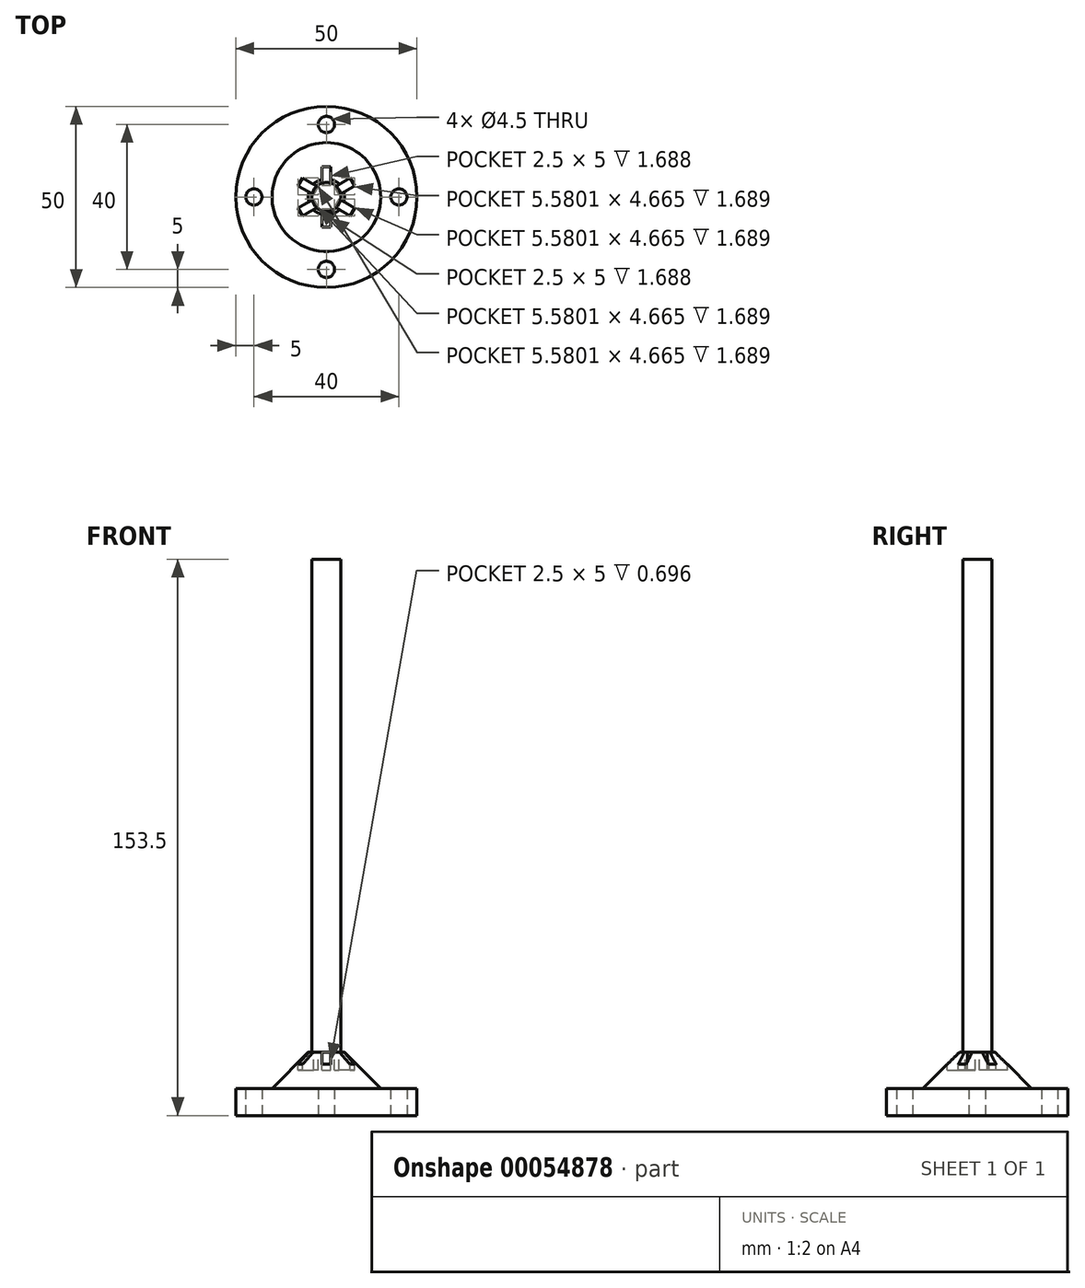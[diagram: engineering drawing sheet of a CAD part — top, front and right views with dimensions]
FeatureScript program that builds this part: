
annotation { "Feature Type Name" : "Feature", "Feature Type Description" : "" }
export const myFeature = defineFeature(function(context is Context, id is Id, definition is map)
    precondition{}
    {
        {
            var Q0;
            Q0=qCreatedBy(makeId("Top.planeOp"),FACE);
            var sketch = newSketch(context, id + "F0", { "sketchPlane" : qUnion([Q0])});
            skCircle(sketch, "E0", {"center": v(0, 0) * mm, "radius": 4 * mm});
            skSolve(sketch);
        }
        {
            var Q0;
            Q0=makeQuery(id+"F0.imprint","IMPRINT",FACE,{"disambiguationData":[TD([[makeQuery(id+"F0.imprint","IMPRINT",EDGE,{"derivedFrom":sQuery(id+"F0.wireOp",EDGE,"E0")}),1.0]])]});
            extrude(context, id + "F1", {"entities" : qUnion([Q0]), "depth" : 136 * mm});
        }
        {
            var Q0;
            Q0=qCreatedBy(makeId("Top.planeOp"),FACE);
            var sketch = newSketch(context, id + "F2", { "sketchPlane" : qUnion([Q0])});
            skCircle(sketch, "E1", {"center": v(0, 0) * mm, "radius": 15 * mm});
            skSolve(sketch);
        }
        {
            var Q0;
            Q0=makeQuery(id+"F2.imprint","IMPRINT",FACE,{"disambiguationData":[TD([[makeQuery(id+"F2.imprint","IMPRINT",EDGE,{"derivedFrom":sQuery(id+"F2.wireOp",EDGE,"E1")}),1.0]])]});
            extrude(context, id + "F3", {"entities" : qUnion([Q0]), "operationType" : NewBodyOperationType.ADD, "oppositeDirection" : true, "depth" : 10 * mm});
        }
        {
            var Q0;
            Q0=makeQuery(id+"F3.opExtrude","CAP_EDGE",EDGE,{"disambiguationData":[OSD([sQuery(id+"F2.wireOp",EDGE,"E1")])],"isStart":true});
            chamfer(context, id + "F4", {"entities" : qUnion([Q0]), "width" : 10 * mm, "tangentPropagation" : true});
        }
        {
            var Q0;
            Q0=makeQuery(id+"F3.opExtrude","CAP_FACE",FACE,{"disambiguationData":[OSD([sQuery(id+"F2.wireOp",EDGE,"E1")])],"isStart":false});
            var sketch = newSketch(context, id + "F5", { "sketchPlane" : qUnion([Q0])});
            skCircle(sketch, "E2", {"center": v(0, 0) * mm, "radius": 25 * mm});
            skSolve(sketch);
        }
        {
            var Q0;
            Q0=makeQuery(id+"F5.imprint","IMPRINT",FACE,{"disambiguationData":[TD([[makeQuery(id+"F5.imprint","IMPRINT",EDGE,{"derivedFrom":sQuery(id+"F5.wireOp",EDGE,"E2")}),1.0]])]});
            var Q1;
            {var subQ0=sQuery(id+"F2.wireOp",EDGE,"E1");Q1=makeQuery(id+"F5.imprint","IMPRINT",FACE,{"disambiguationData":[TD([[makeQuery(id+"F5.imprint","IMPRINT",EDGE,{"derivedFrom":makeQuery(id+"F4.opChamfer","BLEND_EDGE",EDGE,{"blendedFrom":[makeQuery(id+"F3.opExtrude","CAP_EDGE",EDGE,{"disambiguationData":[OSD([subQ0])],"isStart":true}),makeQuery(id+"F3.opExtrude","CAP_FACE",FACE,{"disambiguationData":[OSD([subQ0])],"isStart":false})],"blendedInto":[makeQuery(id+"F3.opExtrude","CAP_FACE",FACE,{"disambiguationData":[OSD([subQ0])],"isStart":false})]})}),-1.0]])]});}
            extrude(context, id + "F6", {"entities" : qUnion([Q0, Q1]), "depth" : 7.5 * mm});
        }
        {
            var Q0;
            Q0=makeQuery(id+"F6.opExtrude","CAP_FACE",FACE,{"disambiguationData":[OSD([sQuery(id+"F2.wireOp",EDGE,"E1"),sQuery(id+"F5.wireOp",EDGE,"E2")])],"isStart":false});
            var sketch = newSketch(context, id + "F7", { "sketchPlane" : qUnion([Q0])});
            skCircle(sketch, "E3", {"center": v(0, 20) * mm, "radius": 2.25 * mm});
            skCircle(sketch, "E4.1.0", {"center": v(20, 0) * mm, "radius": 2.25 * mm});
            skCircle(sketch, "E4.2.0", {"center": v(0, -20) * mm, "radius": 2.25 * mm});
            skPoint(sketch, "E4.center", {"position": v(0, 0) * mm});
            skLineSegment(sketch, "E4.anchor1", {"start": v(0, 0) * mm, "end": v(0, 20) * mm, "construction": true});
            skLineSegment(sketch, "E4.anchor2", {"start": v(0, 0) * mm, "end": v(-20, 0) * mm, "construction": true});
            skCircle(sketch, "E5.1.3.0", {"center": v(-20, 0) * mm, "radius": 2.25 * mm});
            skSolve(sketch);
        }
        {
            var Q0;
            Q0=makeQuery(id+"F7.imprint","IMPRINT",FACE,{"disambiguationData":[TD([[makeQuery(id+"F7.imprint","IMPRINT",EDGE,{"derivedFrom":sQuery(id+"F7.wireOp",EDGE,"E5.1.3.0")}),1.0]])]});
            var Q1;
            Q1=makeQuery(id+"F7.imprint","IMPRINT",FACE,{"disambiguationData":[TD([[makeQuery(id+"F7.imprint","IMPRINT",EDGE,{"derivedFrom":sQuery(id+"F7.wireOp",EDGE,"E3")}),1.0]])]});
            var Q2;
            Q2=makeQuery(id+"F7.imprint","IMPRINT",FACE,{"disambiguationData":[TD([[makeQuery(id+"F7.imprint","IMPRINT",EDGE,{"derivedFrom":sQuery(id+"F7.wireOp",EDGE,"E4.1.0")}),1.0]])]});
            var Q3;
            Q3=makeQuery(id+"F7.imprint","IMPRINT",FACE,{"disambiguationData":[TD([[makeQuery(id+"F7.imprint","IMPRINT",EDGE,{"derivedFrom":sQuery(id+"F7.wireOp",EDGE,"E4.2.0")}),1.0]])]});
            extrude(context, id + "F8", {"entities" : qUnion([Q0, Q1, Q2, Q3]), "operationType" : NewBodyOperationType.REMOVE, "endBound" : BoundingType.THROUGH_ALL, "oppositeDirection" : true, "depth" : 25 * mm});
        }
        {
            var Q0;
            Q0=makeQuery(id+"F3.opExtrude","CAP_FACE",FACE,{"disambiguationData":[OSD([sQuery(id+"F2.wireOp",EDGE,"E1")])],"isStart":true});
            var sketch = newSketch(context, id + "F9", { "sketchPlane" : qUnion([Q0])});
            skLineSegment(sketch, "E6.bottom", {"start": v(-1.25, 8.3) * mm, "end": v(1.25, 8.3) * mm});
            skLineSegment(sketch, "E6.top", {"start": v(-1.25, 3.3) * mm, "end": v(1.25, 3.3) * mm});
            skLineSegment(sketch, "E6.left", {"start": v(-1.25, 8.3) * mm, "end": v(-1.25, 3.3) * mm});
            skLineSegment(sketch, "E6.right", {"start": v(1.25, 8.3) * mm, "end": v(1.25, 3.3) * mm});
            skLineSegment(sketch, "E7.1.0", {"start": v(-6.56, 5.23) * mm, "end": v(-2.23, 2.73) * mm});
            skLineSegment(sketch, "E7.1.1", {"start": v(-7.81, 3.07) * mm, "end": v(-3.48, 0.57) * mm});
            skLineSegment(sketch, "E7.1.2", {"start": v(-3.48, 0.57) * mm, "end": v(-2.23, 2.73) * mm});
            skLineSegment(sketch, "E7.1.3", {"start": v(-7.81, 3.07) * mm, "end": v(-6.56, 5.23) * mm});
            skLineSegment(sketch, "E7.2.0", {"start": v(-7.81, -3.07) * mm, "end": v(-3.48, -0.57) * mm});
            skLineSegment(sketch, "E7.2.1", {"start": v(-6.56, -5.23) * mm, "end": v(-2.23, -2.73) * mm});
            skLineSegment(sketch, "E7.2.2", {"start": v(-2.23, -2.73) * mm, "end": v(-3.48, -0.57) * mm});
            skLineSegment(sketch, "E7.2.3", {"start": v(-6.56, -5.23) * mm, "end": v(-7.81, -3.07) * mm});
            skLineSegment(sketch, "E7.3.0", {"start": v(-1.25, -8.3) * mm, "end": v(-1.25, -3.3) * mm});
            skLineSegment(sketch, "E7.3.1", {"start": v(1.25, -8.3) * mm, "end": v(1.25, -3.3) * mm});
            skLineSegment(sketch, "E7.3.2", {"start": v(1.25, -3.3) * mm, "end": v(-1.25, -3.3) * mm});
            skLineSegment(sketch, "E7.3.3", {"start": v(1.25, -8.3) * mm, "end": v(-1.25, -8.3) * mm});
            skLineSegment(sketch, "E7.4.0", {"start": v(6.56, -5.23) * mm, "end": v(2.23, -2.73) * mm});
            skLineSegment(sketch, "E7.4.1", {"start": v(7.81, -3.07) * mm, "end": v(3.48, -0.57) * mm});
            skLineSegment(sketch, "E7.4.2", {"start": v(3.48, -0.57) * mm, "end": v(2.23, -2.73) * mm});
            skLineSegment(sketch, "E7.4.3", {"start": v(7.81, -3.07) * mm, "end": v(6.56, -5.23) * mm});
            skLineSegment(sketch, "E7.5.0", {"start": v(7.81, 3.07) * mm, "end": v(3.48, 0.57) * mm});
            skLineSegment(sketch, "E7.5.1", {"start": v(6.56, 5.23) * mm, "end": v(2.23, 2.73) * mm});
            skLineSegment(sketch, "E7.5.2", {"start": v(2.23, 2.73) * mm, "end": v(3.48, 0.57) * mm});
            skLineSegment(sketch, "E7.5.3", {"start": v(6.56, 5.23) * mm, "end": v(7.81, 3.07) * mm});
            skPoint(sketch, "E7.center", {"position": v(0, 0) * mm});
            skSolve(sketch);
        }
        {
            var Q0;
            Q0 = qSketchRegion(id + "F9", true);
            extrude(context, id + "F10", {"entities" : qUnion([Q0]), "operationType" : NewBodyOperationType.REMOVE, "oppositeDirection" : true, "depth" : 5 * mm});
        }
        {
            var Q0;
            Q0=makeQuery(id+"F6.opExtrude","CAP_FACE",FACE,{"disambiguationData":[OSD([sQuery(id+"F5.wireOp",EDGE,"E2")])],"isStart":false});
            var sketch = newSketch(context, id + "F11", { "sketchPlane" : qUnion([Q0])});
            skCircle(sketch, "E8", {"center": v(0, 0) * mm, "radius": 1 * mm});
            skSolve(sketch);
        }
    });
